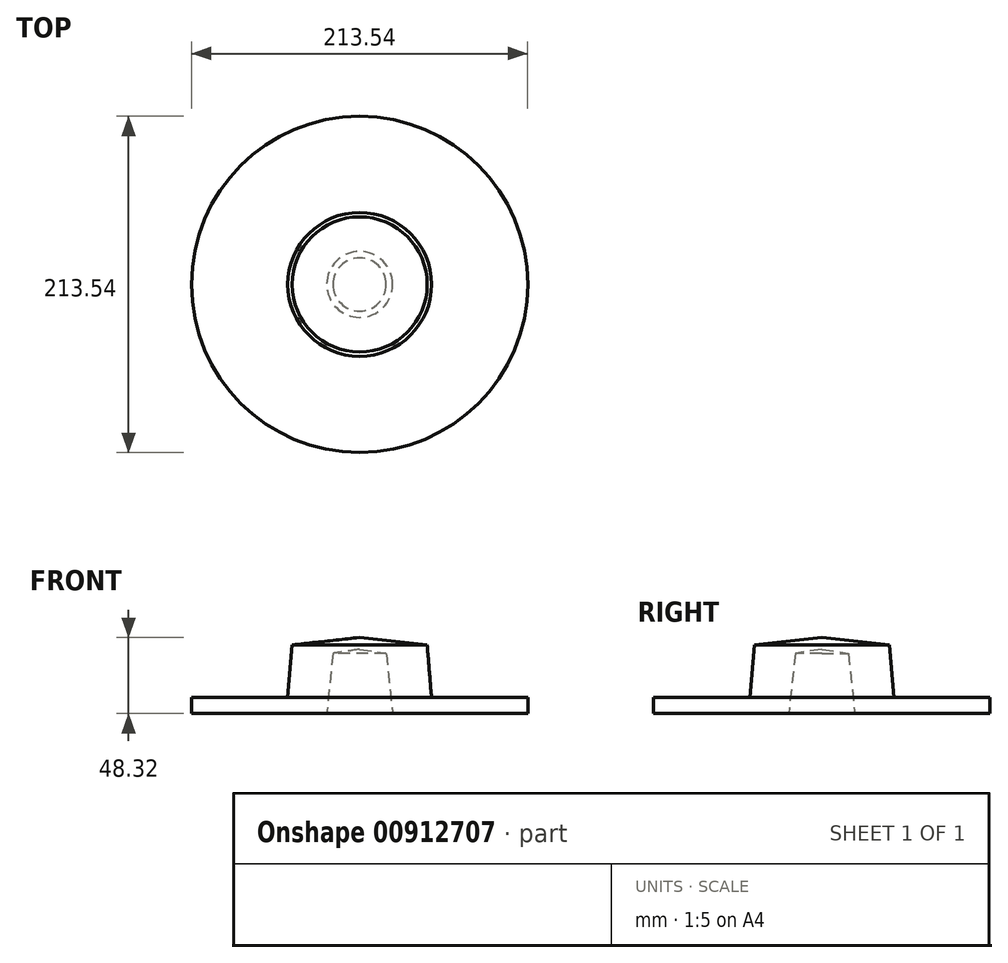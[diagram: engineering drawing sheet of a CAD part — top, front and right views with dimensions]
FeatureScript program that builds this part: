
annotation { "Feature Type Name" : "Feature", "Feature Type Description" : "" }
export const myFeature = defineFeature(function(context is Context, id is Id, definition is map)
    precondition{}
    {
        {
            var Q0;
            Q0=qCreatedBy(makeId("Front.planeOp"),FACE);
            var sketch = newSketch(context, id + "F0", { "sketchPlane" : qUnion([Q0])});
            skLineSegment(sketch, "E0", {"start": v(29.14, 0) * mm, "end": v(106.77, 0) * mm});
            skLineSegment(sketch, "E1", {"start": v(106.77, 0) * mm, "end": v(106.77, 10.32) * mm});
            skLineSegment(sketch, "E2", {"start": v(106.77, 10.32) * mm, "end": v(45.65, 10.32) * mm});
            skLineSegment(sketch, "E3", {"start": v(45.65, 10.32) * mm, "end": v(42.9, 43.6) * mm});
            skLineSegment(sketch, "E4", {"start": v(42.9, 43.6) * mm, "end": v(0, 48.32) * mm});
            skLineSegment(sketch, "E5", {"start": v(0, 48.32) * mm, "end": v(0, 40.83) * mm});
            skLineSegment(sketch, "E6", {"start": v(0, 40.83) * mm, "end": v(16.9, 38.27) * mm});
            skLineSegment(sketch, "E7", {"start": v(16.9, 38.27) * mm, "end": v(20.92, 0) * mm});
            skLineSegment(sketch, "E8", {"start": v(20.92, 0) * mm, "end": v(29.14, 0) * mm});
            skSolve(sketch);
        }
        {
            var Q0;
            Q0=makeQuery(id+"F0.imprint","IMPRINT",FACE,{"disambiguationData":[TD([[makeQuery(id+"F0.imprint","IMPRINT",EDGE,{"derivedFrom":sQuery(id+"F0.wireOp",EDGE,"E0")}),1.0]])]});
            var Q1;
            Q1=sQuery(id+"F0.wireOp",EDGE,"E5");
            revolve(context, id + "F1", {"surfaceOperationType" : NewSurfaceOperationType.NEW, "entities" : qUnion([Q0]), "axis" : qUnion([Q1]), "revolveType" : RevolveType.FULL});
        }
    });
